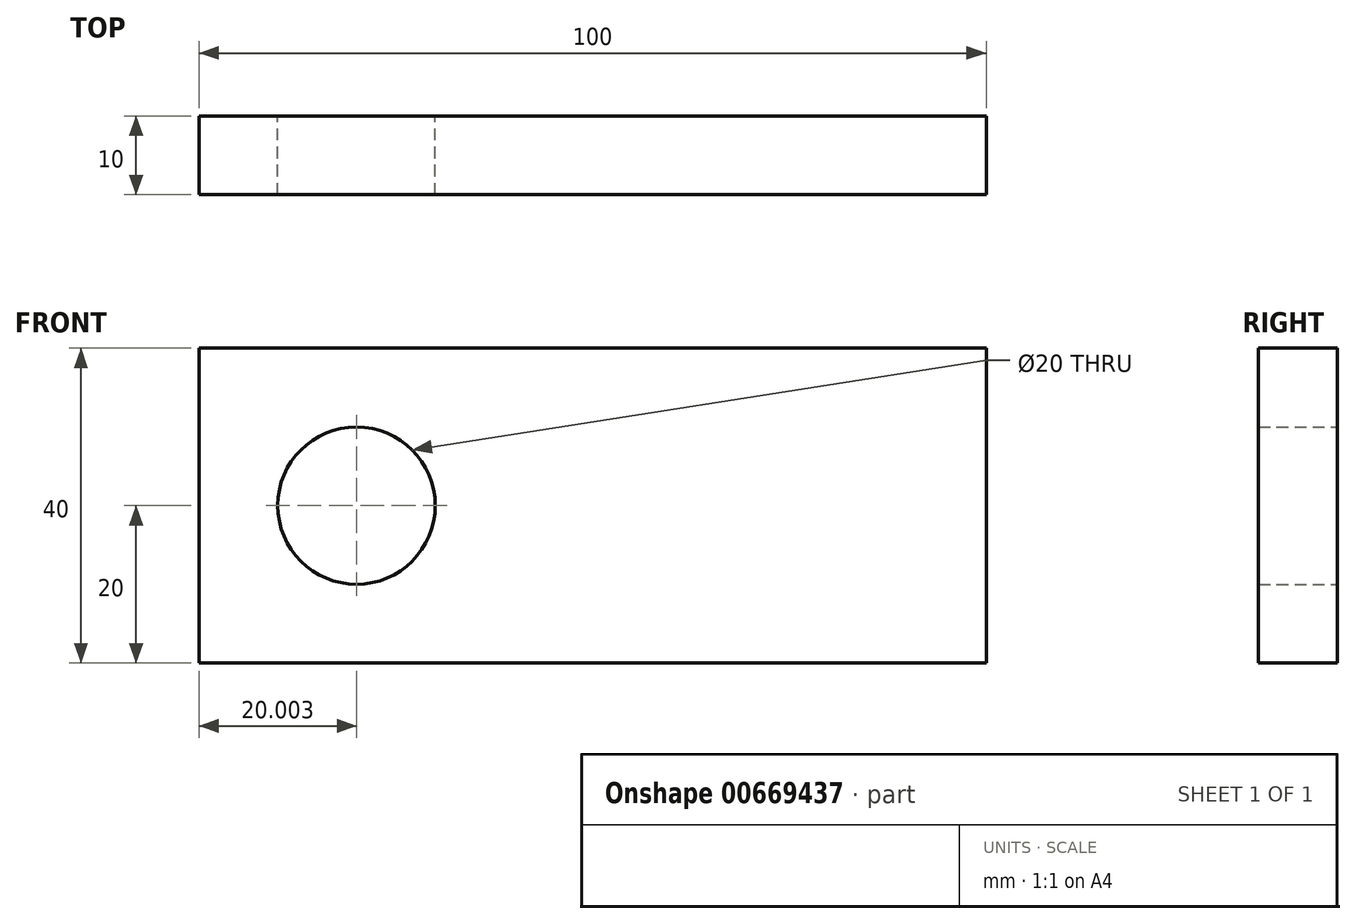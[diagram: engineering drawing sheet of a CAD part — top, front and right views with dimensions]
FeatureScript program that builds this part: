
annotation { "Feature Type Name" : "Feature", "Feature Type Description" : "" }
export const myFeature = defineFeature(function(context is Context, id is Id, definition is map)
    precondition{}
    {
        {
            var Q0;
            Q0=qCreatedBy(makeId("Front.planeOp"),FACE);
            var sketch = newSketch(context, id + "F0", { "sketchPlane" : qUnion([Q0])});
            skLineSegment(sketch, "E0.bottom", {"start": v(-62.8, 51.72) * mm, "end": v(37.2, 51.72) * mm});
            skLineSegment(sketch, "E0.top", {"start": v(-62.8, 11.72) * mm, "end": v(37.2, 11.72) * mm});
            skLineSegment(sketch, "E0.left", {"start": v(-62.8, 51.72) * mm, "end": v(-62.8, 11.72) * mm});
            skLineSegment(sketch, "E0.right", {"start": v(37.2, 51.72) * mm, "end": v(37.2, 11.72) * mm});
            skCircle(sketch, "E1", {"center": v(-42.8, 31.72) * mm, "radius": 10 * mm});
            skSolve(sketch);
        }
        {
            var Q0;
            Q0 = qSketchRegion(id + "F0", true);
            extrude(context, id + "F1", {"entities" : qUnion([Q0]), "depth" : 10 * mm, "offsetDistance" : 25 * mm});
        }
    });
